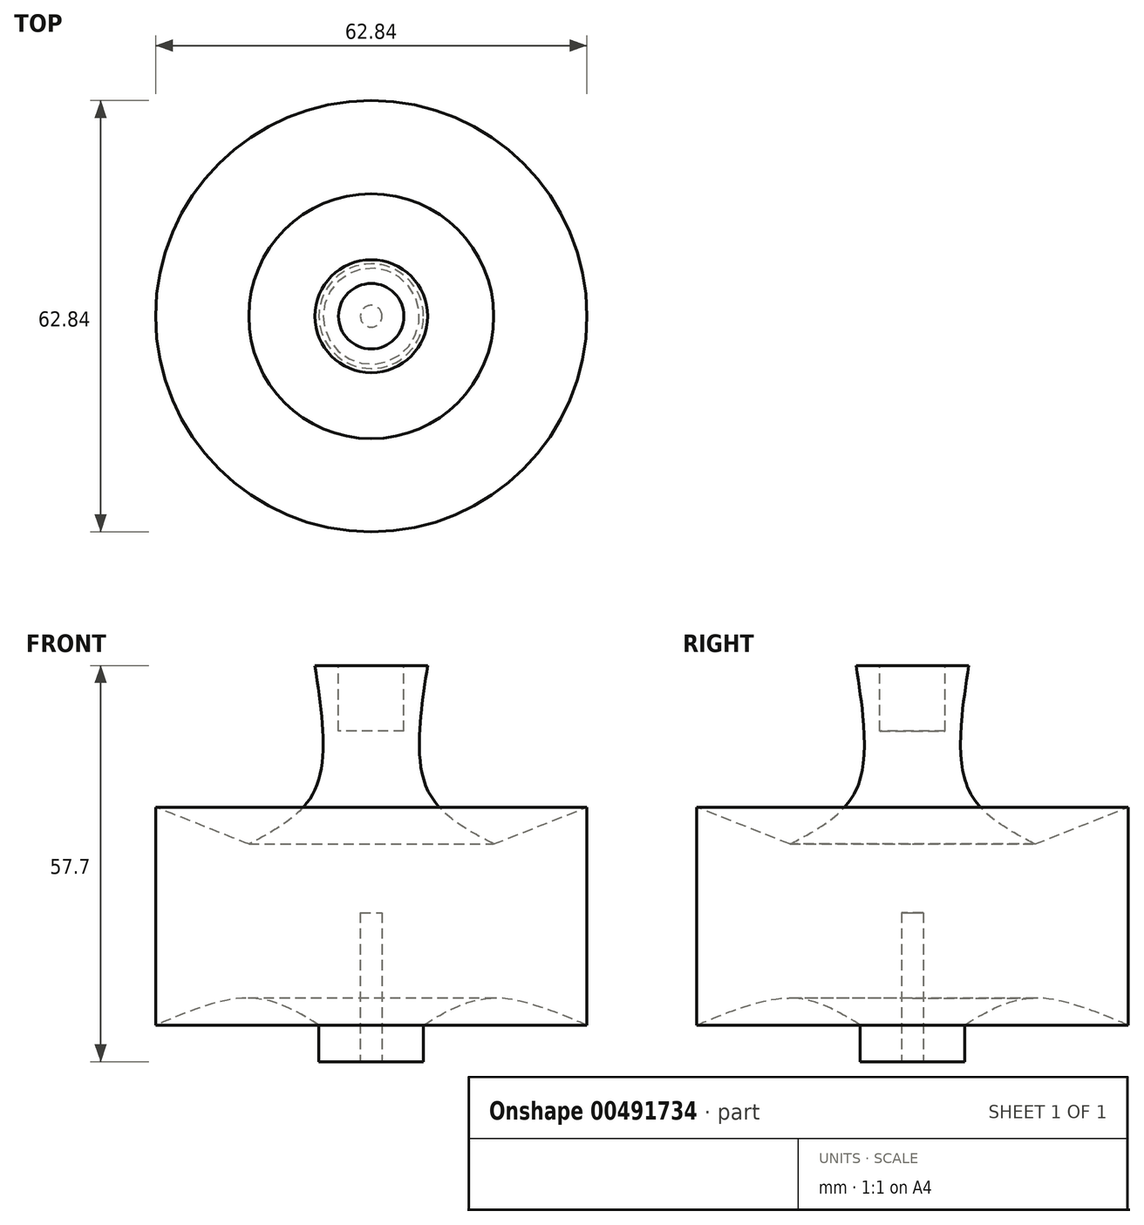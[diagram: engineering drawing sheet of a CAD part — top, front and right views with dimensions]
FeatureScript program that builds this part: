
annotation { "Feature Type Name" : "Feature", "Feature Type Description" : "" }
export const myFeature = defineFeature(function(context is Context, id is Id, definition is map)
    precondition{}
    {
        {
            var Q0;
            Q0=qCreatedBy(makeId("Front.planeOp"),FACE);
            var sketch = newSketch(context, id + "F0", { "sketchPlane" : qUnion([Q0])});
            skLineSegment(sketch, "E0", {"start": v(0, 0) * mm, "end": v(7.62, 0) * mm});
            skLineSegment(sketch, "E1", {"start": v(7.62, 0) * mm, "end": v(7.62, 5.33) * mm});
            skFitSpline(sketch, "E2", {"points": [v(7.62, 5.33) * mm, v(17.32, 9.25) * mm, v(31.42, 5.33) * mm], "startDerivative": vector(18.93, 11.94) * mm, "endDerivative": vector(27.2, -11.18) * mm});
            skLineSegment(sketch, "E3", {"start": v(31.42, 5.33) * mm, "end": v(31.42, 37.08) * mm});
            skLineSegment(sketch, "E4", {"start": v(0, 0) * mm, "end": v(0, 57.7) * mm});
            skLineSegment(sketch, "E5", {"start": v(0, 57.7) * mm, "end": v(8.22, 57.7) * mm});
            skLineSegment(sketch, "E6", {"start": v(31.42, 37.08) * mm, "end": v(17.84, 31.7) * mm});
            skFitSpline(sketch, "E7", {"points": [v(8.22, 57.7) * mm, v(8.22, 39.55) * mm, v(17.84, 31.7) * mm], "startDerivative": vector(-5.81, -37.47) * mm, "endDerivative": vector(26.05, -13.77) * mm});
            skSolve(sketch);
        }
        {
            var Q0;
            Q0=makeQuery(id+"F0.imprint","IMPRINT",FACE,{"disambiguationData":[TD([[makeQuery(id+"F0.imprint","IMPRINT",EDGE,{"derivedFrom":sQuery(id+"F0.wireOp",EDGE,"E0")}),1.0]])]});
            var Q1;
            Q1=sQuery(id+"F0.wireOp",EDGE,"E4");
            revolve(context, id + "F1", {"entities" : qUnion([Q0]), "axis" : qUnion([Q1]), "revolveType" : RevolveType.FULL});
        }
        {
            var Q0;
            Q0=makeQuery(id+"F1.opRevolve","SWEPT_FACE",FACE,{"disambiguationData":[OSD([sQuery(id+"F0.wireOp",EDGE,"E0")])]});
            var sketch = newSketch(context, id + "F2", { "sketchPlane" : qUnion([Q0])});
            skCircle(sketch, "E8", {"center": v(0, 0) * mm, "radius": 1.59 * mm});
            skSolve(sketch);
        }
        {
            var Q0;
            Q0=makeQuery(id+"F2.imprint","IMPRINT",FACE,{"disambiguationData":[TD([[makeQuery(id+"F2.imprint","IMPRINT",EDGE,{"derivedFrom":sQuery(id+"F2.wireOp",EDGE,"E8")}),1.0]])]});
            extrude(context, id + "F3", {"entities" : qUnion([Q0]), "operationType" : NewBodyOperationType.REMOVE, "oppositeDirection" : true, "depth" : 21.72 * mm});
        }
        {
            var Q0;
            Q0=makeQuery(id+"F1.opRevolve","SWEPT_FACE",FACE,{"disambiguationData":[OSD([sQuery(id+"F0.wireOp",EDGE,"E5")])]});
            var sketch = newSketch(context, id + "F4", { "sketchPlane" : qUnion([Q0])});
            skCircle(sketch, "E9", {"center": v(0, 0) * mm, "radius": 4.76 * mm});
            skSolve(sketch);
        }
        {
            var Q0;
            Q0 = qSketchRegion(id + "F4", true);
            extrude(context, id + "F5", {"entities" : qUnion([Q0]), "operationType" : NewBodyOperationType.REMOVE, "oppositeDirection" : true, "depth" : 9.52 * mm});
        }
    });
